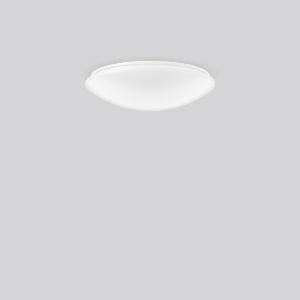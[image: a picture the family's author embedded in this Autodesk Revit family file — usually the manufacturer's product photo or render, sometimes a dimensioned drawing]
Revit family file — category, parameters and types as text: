
# Revit family: flat_polymero_672056_002_5_8a26
name_source: partatom
category: Lighting Fixtures
units: mm (PartAtom-declared; Revit-internal decimal feet)

## family parameters
Cut with Voids When Loaded = No
Host = Face
Light Source = No
Part Type = Normal
Room Calculation Point = No
Round Connector Dimension = Use Diameter
Shared = No

## types (1)
- FLAT POLYMERO (1 x LED Modul 840, 1450 lm, 4000)
    Apparent Load = 14 VA
    CIE Flux Codes = 43 72 90 88 100
    Color Rendering = 80
    Color Temperature = 4000
    Default Elevation = 1800 mm
    Description = Series: FLAT POLYMERO
Decorative round surface-mounted luminaire. For escape route illumination. Base: metal, powder-coated. Diffuser made of non-yellowing plastic (PMMA), opal. Diffuser fastening: patented push system. Suitable for Ceiling mounting, Wall (surface). Driver integrated. 
Colour: white
Diameter: 360 mm
Height: 100 mm
Weight: 1.34 kg
Operating mode: maintained power mode
Lamp: LED
Socket: without socket
Colour temperature: 4000K
Colour rendering index (CRI): 80
System power: 14 W
Rated luminous flux: 1450 lm
Luminous flux, emergency: 1450 lm
System power, emergency: 14 W
Control gear: Regulated power supply
Protection class: I
Type of protection: IP 40
    Height = 100 mm  [stored 0.328084 ft]
    Lamp = 1 x LED Modul 840
    Lamp Light Flux = 1450 lm
    Lamp count = 1
    Length = 360 mm
    Lifetime = 50000 h
    Luminous efficacy = 104 lm/W
    Manufacturer = RZB
    ModVariant = No
    Model = 672056.002.5
    Mounting Place = Ceiling, Wall
    Mounting Type = Surface mounted
    Number of Poles = 1
    OnlyDefault = Yes
    Power Factor = 1
    Product Name = FLAT POLYMERO
    Product group = Surface mounted ceiling and wall luminaires
    ProductGroupID = 305
    Protection Class = Protection class I
    Protection Degree = IP 40
    RLX_Detail_Level = 1
    RLX_Emergency_Light_Flux = 0 lm
    RLX_Emergency_Type = 0
    RLX_Emergency_Type_DB = No
    RlxData = <blob elided: 76225 chars, md5=c87ddbe6>
    Socket = socket
    Standby Power = 0 W
    System Light Flux = 1450 lm
    System Power = 14 W
    Type Comments = ALEA SPOT
    Type Image = 311523.002.1.jpg
    URL = http://relux.com
    VarID = ---
    Voltage = 230 V
    Voltage Range = 220-240 V
    Weight = 0.00 kg
    Width = 0 mm  [stored 0 ft]

note: [stored X ft] marks values corroborated as IEEE doubles in the binary element streams (Revit-internal decimal feet)

## geometry (parser evidence)
native form markers: Blend x4, Sweep x11
no freeform markers — native parametric forms only
